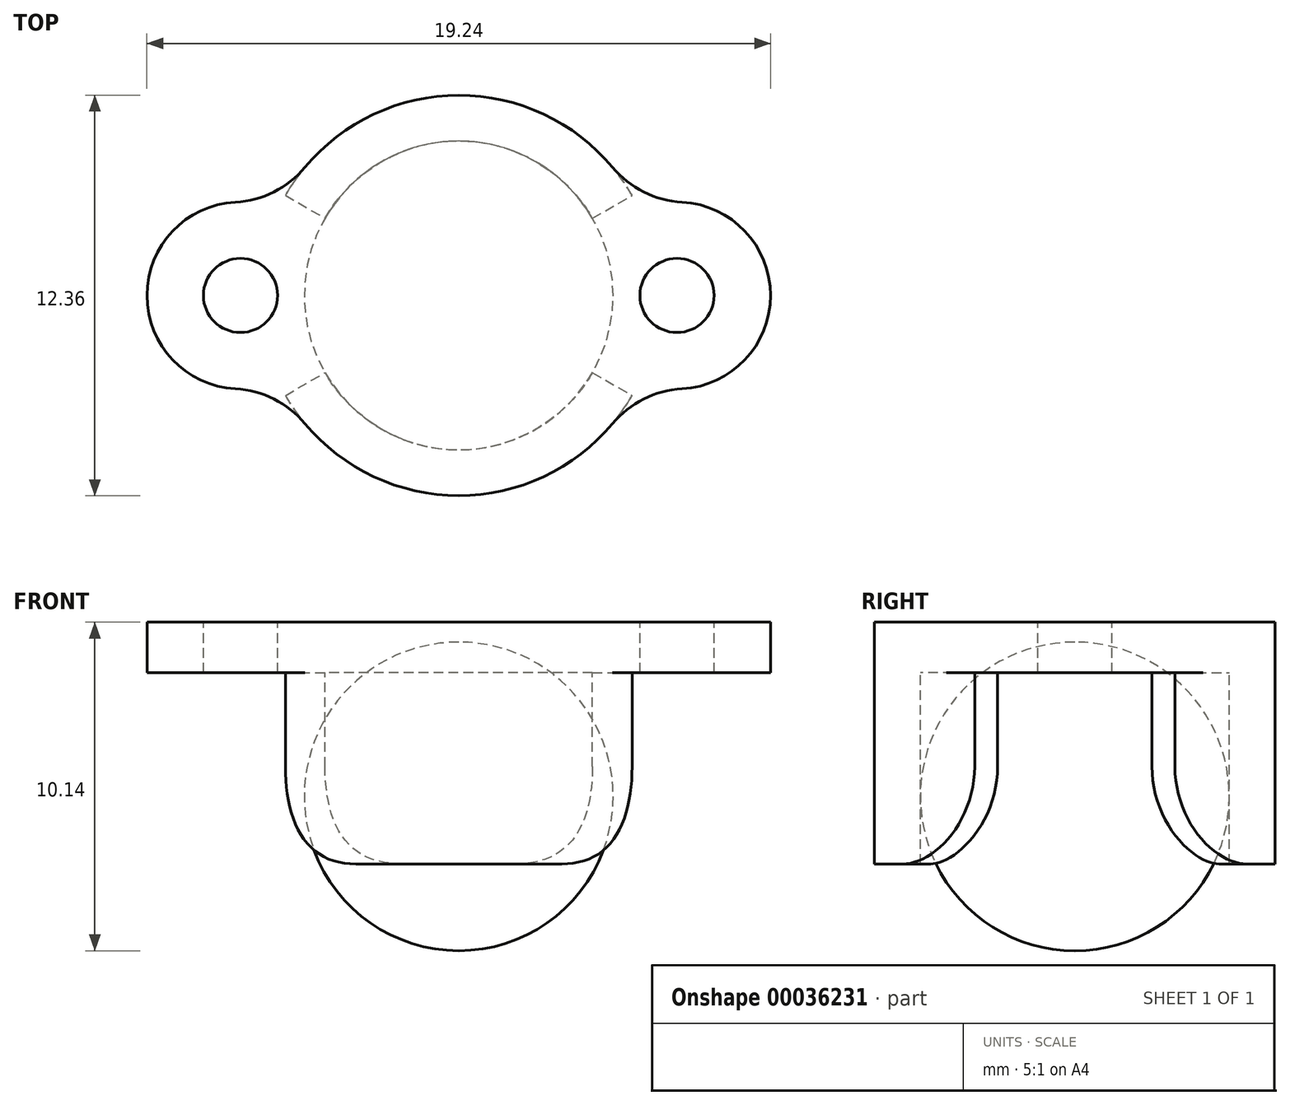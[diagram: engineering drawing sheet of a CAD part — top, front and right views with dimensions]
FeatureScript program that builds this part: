
annotation { "Feature Type Name" : "Feature", "Feature Type Description" : "" }
export const myFeature = defineFeature(function(context is Context, id is Id, definition is map)
    precondition{}
    {
        {
            var Q0;
            Q0=qCreatedBy(makeId("Top.planeOp"),FACE);
            var sketch = newSketch(context, id + "F0", { "sketchPlane" : qUnion([Q0])});
            skArc(sketch, "E0", {"start": v(4.74, 3.95) * mm, "mid": v(0, 6.17) * mm, "end": v(-4.74, 3.95) * mm});
            skCircle(sketch, "E1", {"center": v(-6.73, 0) * mm, "radius": 1.14 * mm});
            skCircle(sketch, "E2", {"center": v(6.73, 0) * mm, "radius": 1.14 * mm});
            skArc(sketch, "E3", {"start": v(6.89, -2.88) * mm, "mid": v(9.62, 0) * mm, "end": v(6.89, 2.88) * mm});
            skArc(sketch, "E4", {"start": v(-6.89, 2.88) * mm, "mid": v(-9.62, 0) * mm, "end": v(-6.89, -2.88) * mm});
            skArc(sketch, "E5.trimOffspring", {"start": v(-4.74, -3.95) * mm, "mid": v(0, -6.18) * mm, "end": v(4.74, -3.95) * mm});
            skPoint(sketch, "E6.visualSharp", {"position": v(5.58, 2.64) * mm});
            skArc(sketch, "E6.filletArc", {"start": v(4.74, 3.95) * mm, "mid": v(5.7, 3.2) * mm, "end": v(6.89, 2.88) * mm});
            skPoint(sketch, "E7.visualSharp", {"position": v(5.58, -2.64) * mm});
            skArc(sketch, "E7.filletArc", {"start": v(6.89, -2.88) * mm, "mid": v(5.7, -3.2) * mm, "end": v(4.74, -3.95) * mm});
            skPoint(sketch, "E8.visualSharp", {"position": v(-5.58, -2.64) * mm});
            skArc(sketch, "E8.filletArc", {"start": v(-4.74, -3.95) * mm, "mid": v(-5.7, -3.2) * mm, "end": v(-6.89, -2.88) * mm});
            skPoint(sketch, "E9.visualSharp", {"position": v(-5.58, 2.64) * mm});
            skArc(sketch, "E9.filletArc", {"start": v(-6.89, 2.88) * mm, "mid": v(-5.7, 3.2) * mm, "end": v(-4.74, 3.95) * mm});
            skSolve(sketch);
        }
        {
            var Q0;
            Q0=makeQuery(id+"F0.imprint","IMPRINT",FACE,{"disambiguationData":[TD([[makeQuery(id+"F0.imprint","IMPRINT",EDGE,{"derivedFrom":sQuery(id+"F0.wireOp",EDGE,"E0")}),1.0]])]});
            extrude(context, id + "F1", {"entities" : qUnion([Q0]), "oppositeDirection" : true, "depth" : 1.56 * mm});
        }
        {
            var Q0;
            Q0=makeQuery(id+"F1.opExtrude","CAP_FACE",FACE,{"disambiguationData":[OSD([sQuery(id+"F0.wireOp",EDGE,"E0"),sQuery(id+"F0.wireOp",EDGE,"E1"),sQuery(id+"F0.wireOp",EDGE,"E2"),sQuery(id+"F0.wireOp",EDGE,"E3"),sQuery(id+"F0.wireOp",EDGE,"E4"),sQuery(id+"F0.wireOp",EDGE,"E5.trimOffspring"),sQuery(id+"F0.wireOp",EDGE,"E6.filletArc"),sQuery(id+"F0.wireOp",EDGE,"E7.filletArc"),sQuery(id+"F0.wireOp",EDGE,"E8.filletArc"),sQuery(id+"F0.wireOp",EDGE,"E9.filletArc")])],"isStart":false});
            var sketch = newSketch(context, id + "F2", { "sketchPlane" : qUnion([Q0])});
            skArc(sketch, "E10", {"start": v(5.35, 3.09) * mm, "mid": v(0, 6.17) * mm, "end": v(-5.35, 3.09) * mm});
            skArc(sketch, "E11", {"start": v(4.12, 2.38) * mm, "mid": v(0, 4.76) * mm, "end": v(-4.12, 2.38) * mm});
            skLineSegment(sketch, "E12", {"start": v(-5.35, 3.09) * mm, "end": v(-4.12, 2.38) * mm});
            skPoint(sketch, "E12.startSnap0", {"position": v(-5.7, 3.2) * mm});
            skLineSegment(sketch, "E13", {"start": v(4.12, 2.38) * mm, "end": v(5.35, 3.09) * mm});
            skLineSegment(sketch, "E14", {"start": v(0, 0) * mm, "end": v(0, 6.17) * mm, "construction": true});
            skSolve(sketch);
        }
        {
            var Q0;
            Q0=makeQuery(id+"F2.imprint","IMPRINT",FACE,{"disambiguationData":[TD([[makeQuery(id+"F2.imprint","IMPRINT",EDGE,{"derivedFrom":sQuery(id+"F2.wireOp",EDGE,"E11")}),-1.0]])]});
            extrude(context, id + "F3", {"entities" : qUnion([Q0]), "operationType" : NewBodyOperationType.ADD, "depth" : 5.9 * mm});
        }
        {
            var Q0;
            Q0=makeQuery(id+"F1.opExtrude","SWEPT_BODY",BODY,{"disambiguationData":[OSD([sQuery(id+"F0.wireOp",EDGE,"E0"),sQuery(id+"F0.wireOp",EDGE,"E1"),sQuery(id+"F0.wireOp",EDGE,"E2"),sQuery(id+"F0.wireOp",EDGE,"E3"),sQuery(id+"F0.wireOp",EDGE,"E4"),sQuery(id+"F0.wireOp",EDGE,"E5.trimOffspring"),sQuery(id+"F0.wireOp",EDGE,"E6.filletArc"),sQuery(id+"F0.wireOp",EDGE,"E7.filletArc"),sQuery(id+"F0.wireOp",EDGE,"E8.filletArc"),sQuery(id+"F0.wireOp",EDGE,"E9.filletArc")])]});
            var Q1;
            Q1=makeQuery(id+"F3.opExtrude","CAP_FACE",FACE,{"disambiguationData":[OSD([sQuery(id+"F2.wireOp",EDGE,"E10"),sQuery(id+"F2.wireOp",EDGE,"E11"),sQuery(id+"F2.wireOp",EDGE,"E12"),sQuery(id+"F2.wireOp",EDGE,"E13")])],"isStart":false});
            var Q2;
            Q2=qCreatedBy(makeId("Front.planeOp"),FACE);
            mirror(context, id + "F4", {"operationType" : NewBodyOperationType.ADD, "entities" : qUnion([Q0]), "faces" : qUnion([Q1]), "mirrorPlane" : qUnion([Q2])});
        }
        {
            var Q0;
            Q0=qCreatedBy(makeId("Right.planeOp"),FACE);
            var sketch = newSketch(context, id + "F5", { "sketchPlane" : qUnion([Q0])});
            skArc(sketch, "E15", {"start": v(0, -10.14) * mm, "mid": v(4.76, -5.38) * mm, "end": v(0, -0.62) * mm});
            skLineSegment(sketch, "E16", {"start": v(0, -10.14) * mm, "end": v(0, -0.62) * mm});
            skSolve(sketch);
        }
        {
            var Q0;
            Q0=makeQuery(id+"F5.imprint","IMPRINT",FACE,{"disambiguationData":[TD([[makeQuery(id+"F5.imprint","IMPRINT",EDGE,{"derivedFrom":sQuery(id+"F5.wireOp",EDGE,"E15")}),1.0]])]});
            var Q1;
            Q1=sQuery(id+"F5.wireOp",EDGE,"E16");
            revolve(context, id + "F6", {"entities" : qUnion([Q0]), "axis" : qUnion([Q1]), "revolveType" : RevolveType.FULL});
        }
        {
            var Q0;
            Q0=makeQuery(id+"F4.opPattern","COPY",EDGE,{"derivedFrom":makeQuery(id+"F3.opExtrude","CAP_EDGE",EDGE,{"disambiguationData":[OSD([sQuery(id+"F2.wireOp",EDGE,"E13")])],"isStart":false}),"instanceName":"1"});
            var Q1;
            Q1=makeQuery(id+"F3.opExtrude","CAP_EDGE",EDGE,{"disambiguationData":[OSD([sQuery(id+"F2.wireOp",EDGE,"E13")])],"isStart":false});
            var Q2;
            Q2=makeQuery(id+"F4.opPattern","COPY",EDGE,{"derivedFrom":makeQuery(id+"F3.opExtrude","CAP_EDGE",EDGE,{"disambiguationData":[OSD([sQuery(id+"F2.wireOp",EDGE,"E12")])],"isStart":false}),"instanceName":"1"});
            var Q3;
            Q3=makeQuery(id+"F3.opExtrude","CAP_EDGE",EDGE,{"disambiguationData":[OSD([sQuery(id+"F2.wireOp",EDGE,"E12")])],"isStart":false});
            fillet(context, id + "F7", {"entities" : qUnion([Q0, Q1, Q2, Q3]), "radius" : 3 * mm, "tangentPropagation" : true, "allowEdgeOverflow" : false});
        }
    });
